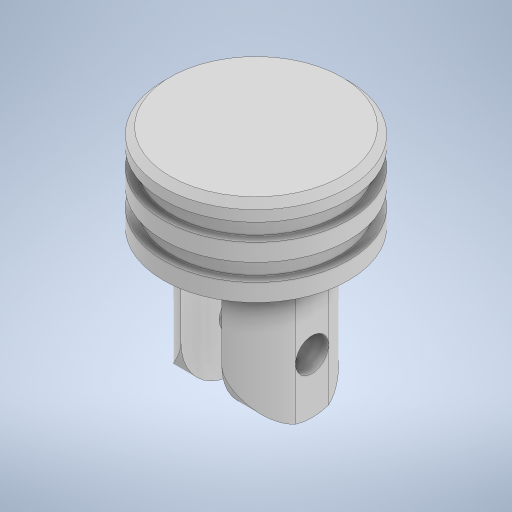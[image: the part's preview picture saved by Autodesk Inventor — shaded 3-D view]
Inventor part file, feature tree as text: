
AUTODESK INVENTOR PART (.ipt)
format: ipt  version: 2023 (Build 270158000, 158)  size: 338,432 bytes
history: native  units: in
note: dims shown in document units (in); Inventor stores cm internally (conversion verified against a paired STEP export)
features: sketch x3, extrude x2, revolve x1, chamfer x1, fillet x1
ambient origin geometry x8: Origin, YZ Plane, XZ Plane, XY Plane, X Axis, Y Axis, Z Axis, Center Point
bodies: Solid1 (feature_tree)
feature tree (8):
  revolve  "Revolution1"  [1 undecoded]
  extrude  "Extrusion2"  Depth=0.132in
  chamfer  "Chamfer1"  Distance=0.132in
  fillet  "Fillet1"  Radius=0.066in
  extrude  "Extrusion3"  Depth=0.125in
  sketch  "Sketch1"  dims[d0=0.7017in d1=0.132in]
  sketch  "Sketch2"  dims[d2=0.066in d3=0.132in]
  sketch  "Sketch3"  dims[d4=0.066in d5=0.132in d6=0.066in d7=0.132in d8=0.066in d9=0.132in d10=90.0deg d18=0.125in d19=1.25in d20=0.0in d21=0.05in d22=0.125in d23=45.0deg d24=0.125in d25=1.25in d26=0.0in]
note: 1 required parameter value undecoded (feature->parameter linkage not recoverable at this tier; creation-order binding heuristic only, values carry confidence <= 0.55)
